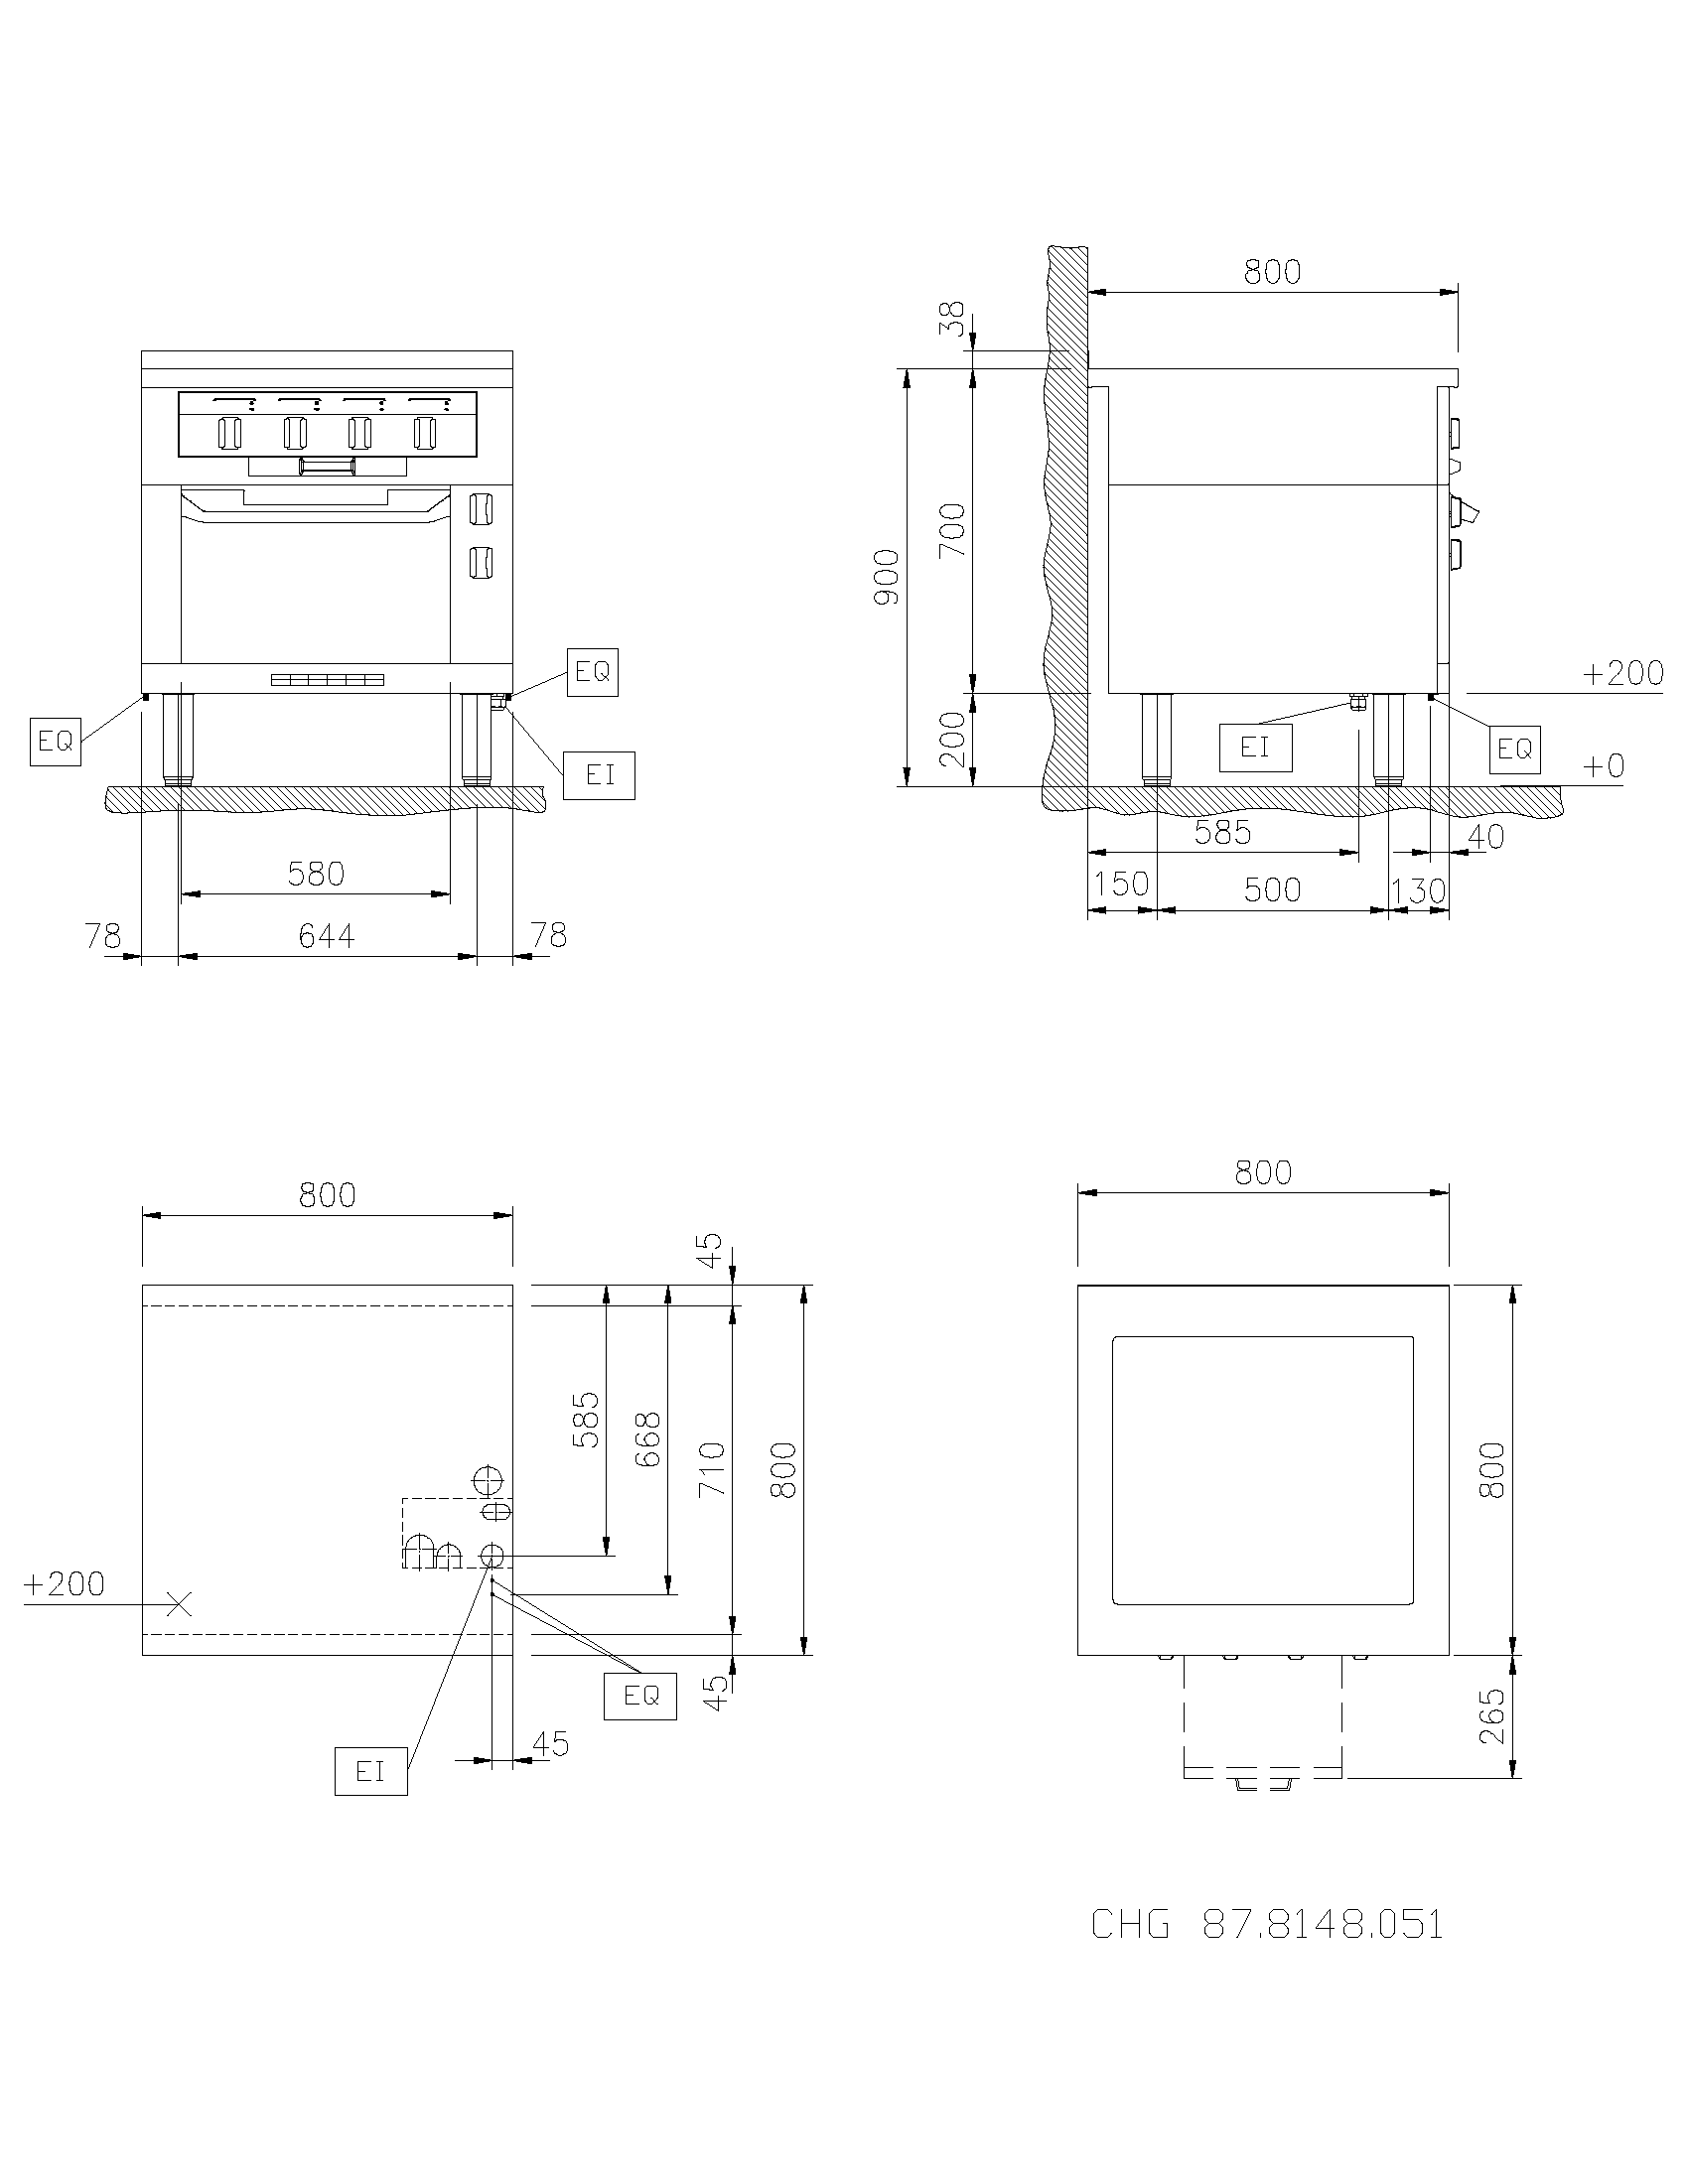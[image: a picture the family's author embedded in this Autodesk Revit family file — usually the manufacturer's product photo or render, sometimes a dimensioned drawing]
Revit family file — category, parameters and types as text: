
# Revit family: QF_ELECTROLUXPROFESSIONAL_588413_MALNECH8AO
name_source: partatom
category: Attrezzature speciali
units: mm (PartAtom-declared; Revit-internal decimal feet)

## family parameters
Basato su piano di lavoro = No
Condiviso = No
Punto di calcolo locali = No
Quota connettore circolare = Usa diametro
Sempre verticale = Sì
Taglio con vuoti quando caricato = No
Tipo di parte = Normale

## types (1)
- Standard
    Accessory = Sì
    Cold Water Size = 0"
    Compressed Air Pressure = 0.00 psi
    Compressed Air Size = 0"
    Compressed Air Volume = 0 GPM
    Condensate Return Size = 0"
    Cycle = 50 Hz
    Depth Actual = 800 mm  [stored 2.62467 ft]
    Descrizione = EL.SOLID TOP,ST.OV,PASS,2S,800X800X700H
    Direct Waste Size = 0"
    Gas Input Pressure = 0.0
    Gas KW = 0
    Gas Size = 0"
    HP = 23.2 HP
    Height Actual = 700 mm  [stored 2.29659 ft]
    Hot Water Size = 0"
    Item Number = 588413
    Length Actual = 800 mm  [stored 2.62467 ft]
    Modello = MALNECH8AO
    Phase = 3
    Produttore = Electrolux Professional
    Prospetto di default = 0 mm  [stored 0 ft]
    Refrigerant Compressor Remote = Sì
    Refrigeration Liquid Line Size = 0 mm  [stored 0 ft]
    Refrigeration Suction Line Size = 0 mm  [stored 0 ft]
    Steam Consumption per Hour = 0
    Steam Supply Maximum Pressure = 0.00 psi
    Steam Supply Minimum Pressure = 0.00 psi
    Steam Supply Size = 0"
    URL = https://www.electroluxprofessional.com
    URL Manufacturer = https://www.electroluxprofessional.com
    Volts = 400 V
    Watts = 17300 W
    Weight = 211.00 kg

note: source unit labels omitted for Gas Input Pressure — the stored unit's dimension contradicts the parameter name (converter mislabeling)

note: [stored X ft] marks values corroborated as IEEE doubles in the binary element streams (Revit-internal decimal feet)

## geometry (parser evidence)
native form markers: Blend x12, Sweep x15
no freeform markers — native parametric forms only
